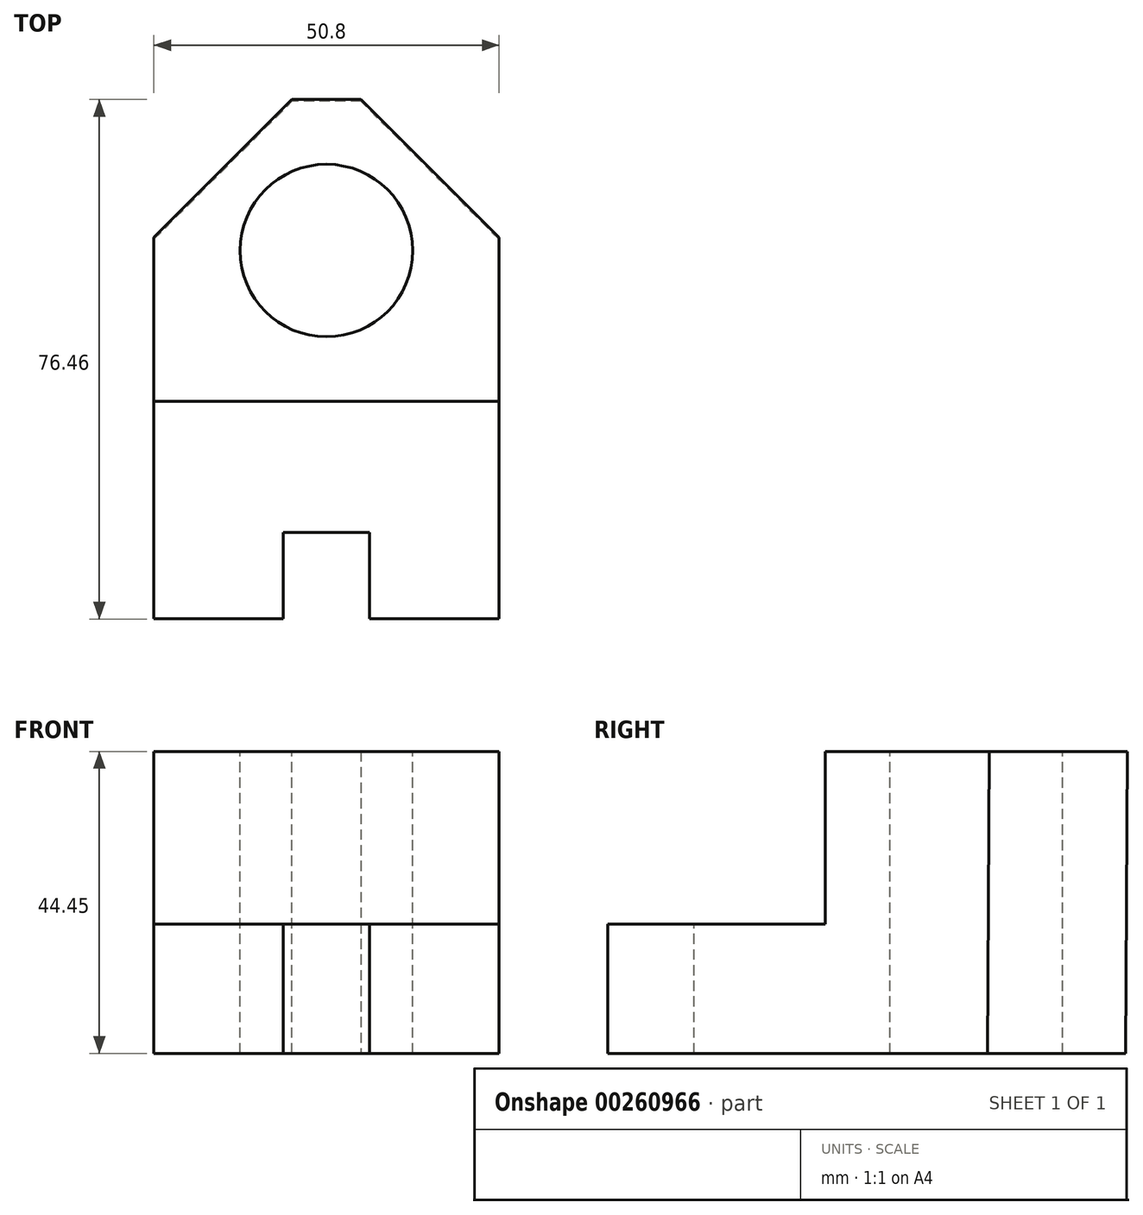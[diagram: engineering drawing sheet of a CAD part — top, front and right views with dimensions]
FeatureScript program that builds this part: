
annotation { "Feature Type Name" : "Feature", "Feature Type Description" : "" }
export const myFeature = defineFeature(function(context is Context, id is Id, definition is map)
    precondition{}
    {
        {
            var Q0;
            Q0=qCreatedBy(makeId("Right.planeOp"),FACE);
            var sketch = newSketch(context, id + "F0", { "sketchPlane" : qUnion([Q0])});
            skLineSegment(sketch, "E0", {"start": v(-40.58, 0) * mm, "end": v(-24.57, 0) * mm});
            skLineSegment(sketch, "E1", {"start": v(-24.57, 0) * mm, "end": v(-8.57, 0) * mm});
            skLineSegment(sketch, "E2", {"start": v(-40.58, 0) * mm, "end": v(-40.58, -19.05) * mm});
            skLineSegment(sketch, "E3", {"start": v(-8.57, 0) * mm, "end": v(-8.57, 25.4) * mm});
            skLineSegment(sketch, "E4", {"start": v(-8.57, 25.4) * mm, "end": v(35.88, 25.4) * mm});
            skLineSegment(sketch, "E5", {"start": v(-40.58, -19.05) * mm, "end": v(35.62, -19.05) * mm});
            skLineSegment(sketch, "E6", {"start": v(35.88, 25.4) * mm, "end": v(35.62, -19.05) * mm});
            skSolve(sketch);
        }
        {
            var Q0;
            Q0=makeQuery(id+"F0.imprint","IMPRINT",FACE,{"disambiguationData":[TD([[makeQuery(id+"F0.imprint","IMPRINT",EDGE,{"derivedFrom":sQuery(id+"F0.wireOp",EDGE,"E0")}),-1.0]])]});
            extrude(context, id + "F1", {"entities" : qUnion([Q0]), "depth" : 50.8 * mm});
        }
        {
            var Q0;
            Q0=makeQuery(id+"F1.opExtrude","SWEPT_FACE",FACE,{"disambiguationData":[OSD([sQuery(id+"F0.wireOp",EDGE,"E4")])]});
            var sketch = newSketch(context, id + "F2", { "sketchPlane" : qUnion([Q0])});
            skLineSegment(sketch, "E7", {"start": v(25.4, 35.88) * mm, "end": v(25.4, 13.65) * mm});
            skPoint(sketch, "E7.endSnap0", {"position": v(50.8, 13.65) * mm});
            skSolve(sketch);
        }
        {
            var Q0;
            Q0=sQuery(id+"F2.wireOp",VERTEX,"E7.end");
            var Q1;
            Q1=makeQuery(id+"F1.opExtrude","SWEPT_BODY",BODY,{"disambiguationData":[OSD([sQuery(id+"F0.wireOp",EDGE,"E0"),sQuery(id+"F0.wireOp",EDGE,"E1"),sQuery(id+"F0.wireOp",EDGE,"E2"),sQuery(id+"F0.wireOp",EDGE,"E3"),sQuery(id+"F0.wireOp",EDGE,"E4"),sQuery(id+"F0.wireOp",EDGE,"E5"),sQuery(id+"F0.wireOp",EDGE,"E6")])]});
            hole(context, id + "F3", {"style" : HoleStyle.SIMPLE, "endStyle" : HoleEndStyle.THROUGH, "holeDiameter" : 25.4 * mm, "tappedDepth" : 12.7 * mm, "tapClearance" : 3, "locations" : qUnion([Q0]), "scope" : qUnion([Q1])});
        }
        {
            var Q0;
            Q0=makeQuery(id+"F1.opExtrude","CAP_EDGE",EDGE,{"disambiguationData":[OSD([sQuery(id+"F0.wireOp",EDGE,"E6")])],"isStart":true});
            var Q1;
            Q1=makeQuery(id+"F1.opExtrude","CAP_EDGE",EDGE,{"disambiguationData":[OSD([sQuery(id+"F0.wireOp",EDGE,"E6")])],"isStart":false});
            chamfer(context, id + "F4", {"entities" : qUnion([Q0, Q1]), "width" : 20.32 * mm, "tangentPropagation" : true});
        }
        {
            var Q0;
            Q0=makeQuery(id+"F1.opExtrude","SWEPT_FACE",FACE,{"disambiguationData":[OSD([sQuery(id+"F0.wireOp",EDGE,"E0"),sQuery(id+"F0.wireOp",EDGE,"E1")])]});
            var sketch = newSketch(context, id + "F5", { "sketchPlane" : qUnion([Q0])});
            skLineSegment(sketch, "E8", {"start": v(0, -40.58) * mm, "end": v(19.05, -40.58) * mm});
            skLineSegment(sketch, "E9", {"start": v(19.05, -40.58) * mm, "end": v(19.05, -27.88) * mm});
            skLineSegment(sketch, "E10", {"start": v(19.05, -27.88) * mm, "end": v(31.75, -27.88) * mm});
            skLineSegment(sketch, "E11", {"start": v(31.75, -27.88) * mm, "end": v(31.75, -40.58) * mm});
            skLineSegment(sketch, "E12", {"start": v(31.75, -40.58) * mm, "end": v(50.8, -40.58) * mm});
            skSolve(sketch);
        }
        {
            var Q0;
            {var subQ0=sQuery(id+"F5.wireOp",EDGE,"E9");Q0=makeQuery(id+"F5.imprint","IMPRINT",FACE,{"disambiguationData":[TD([[makeQuery(id+"F5.imprint","IMPRINT",EDGE,{"derivedFrom":subQ0}),-1.0]])]});}
            extrude(context, id + "F6", {"entities" : qUnion([Q0]), "operationType" : NewBodyOperationType.ADD, "depth" : 0.25 * mm});
        }
        {
            var Q0;
            Q0=makeQuery(id+"F6.opExtrude","CAP_FACE",FACE,{"disambiguationData":[OSD([sQuery(id+"F0.wireOp",EDGE,"E0"),sQuery(id+"F0.wireOp",EDGE,"E2"),sQuery(id+"F5.wireOp",EDGE,"E9"),sQuery(id+"F5.wireOp",EDGE,"E10"),sQuery(id+"F5.wireOp",EDGE,"E11")])],"isStart":false});
            extrude(context, id + "F7", {"entities" : qUnion([Q0]), "operationType" : NewBodyOperationType.REMOVE, "oppositeDirection" : true, "depth" : 35.05 * mm});
        }
    });
